# Revit family: P190780JX-031c_JJW6024HL_Urban_Living_Steam-Oven
name_source: partatom
category: Specialty Equipment
units: mm (PartAtom-declared; Revit-internal decimal feet)

## family parameters
Always vertical = Yes
Cut with Voids When Loaded = No
Enable Cutting in Views = No
Maintain Annotation Orientation = No
Part Type = Normal
Room Calculation Point = No
Round Connector Dimension = Use Diameter
Shared = No
Work Plane-Based = No

## types (1)
- JJW6024HL
    Amps = 0 A
    Body Material = ARCAT - Metal - Steel - Stainless
    Clearance Material = ARCAT - Clearance
    Default Elevation = 0"
    Depth = 20 3/8"
    Description = RISE 60cm Built-In Steam Oven
Four à vapeur encastré RISE™, 60 cm
    Dimension Guide = https://www.whirlpool.com
    Display Panel Material = ARCAT - Metal - Steel - Stainless
    Door Material = ARCAT - Metal - Steel - Stainless
    Family Name = SMALL SPACES - 24" - Steam Oven
    Feature 1 = Emotive Controls
Commandes sensibles
    Feature 2 = STEAM OVEN
FOUR À VAPEUR
    Feature 3 = 1.3 Cu. Ft. Capacity
Capacité de 1,3 pi3
    Glass Material = ARCAT - Glass - Tempered - Black
    Handle Material = ARCAT - Metal - Steel - Gray
    Height = 18 5/16"
    Installation-Fabrication = https://www.whirlpool.com
    Leg Material = ARCAT - Plastic - Black
    Manufacturer = Jenn Air
    Model = JJW6024HL
    Voltage = 0 V
    Width = 23 7/16"

## geometry (parser evidence)
native form markers: Sweep x4
no freeform markers — native parametric forms only
